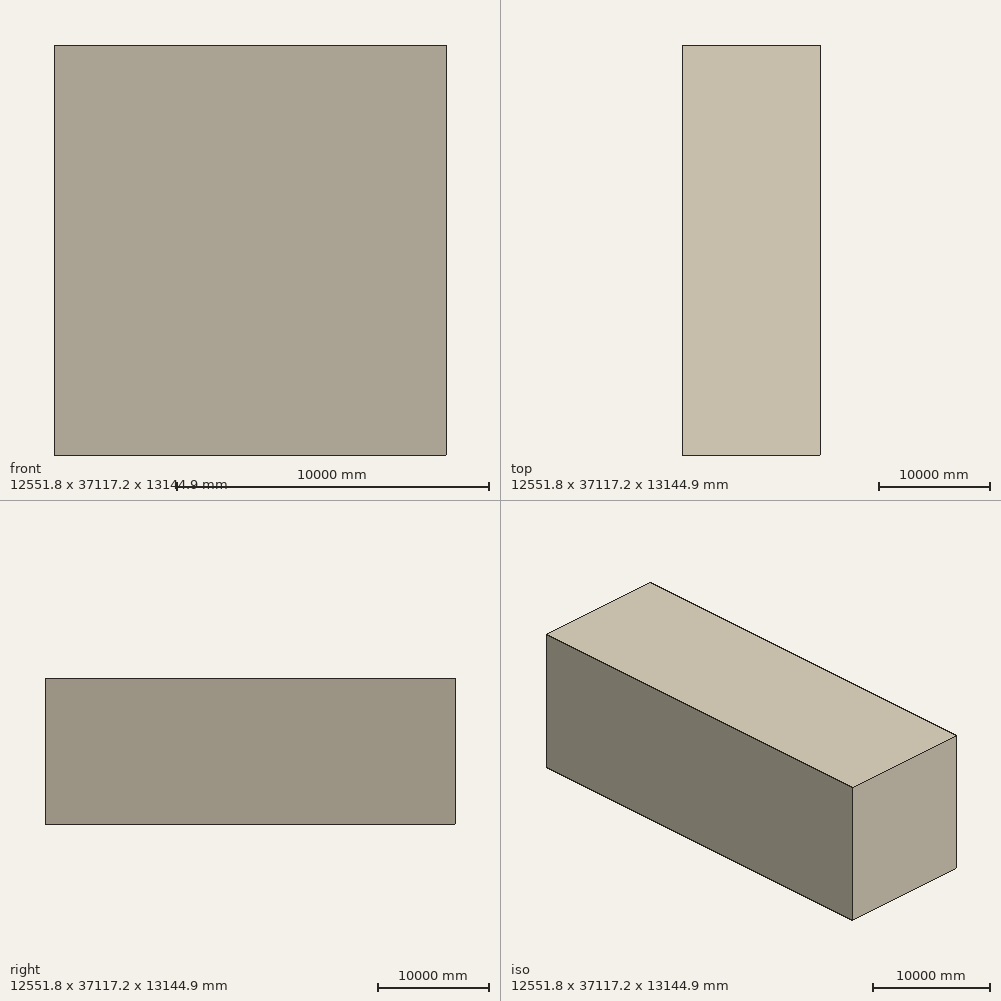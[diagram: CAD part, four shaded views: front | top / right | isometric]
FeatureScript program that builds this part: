
annotation { "Feature Type Name" : "Feature", "Feature Type Description" : "" }
export const myFeature = defineFeature(function(context is Context, id is Id, definition is map)
    precondition{}
    {
        {
            var Q0;
            Q0=qCreatedBy(makeId("Top.planeOp"),FACE);
            var sketch = newSketch(context, id + "F0", { "sketchPlane" : qUnion([Q0])});
            skLineSegment(sketch, "E0.bottom", {"start": v(6275.88, 18558.6) * mm, "end": v(-6275.88, 18558.6) * mm});
            skLineSegment(sketch, "E0.top", {"start": v(6275.88, -18558.6) * mm, "end": v(-6275.88, -18558.6) * mm});
            skLineSegment(sketch, "E0.left", {"start": v(6275.88, -18558.6) * mm, "end": v(6275.88, 18558.6) * mm});
            skLineSegment(sketch, "E0.right", {"start": v(-6275.88, -18558.6) * mm, "end": v(-6275.88, 18558.6) * mm});
            skPoint(sketch, "E0.middle", {"position": v(0, 0) * mm});
            skSolve(sketch);
        }
        {
            var Q0;
            Q0=makeQuery(id+"F0.imprint","IMPRINT",FACE,{"disambiguationData":[TD([[makeQuery(id+"F0.imprint","IMPRINT",EDGE,{"derivedFrom":sQuery(id+"F0.wireOp",EDGE,"E0.bottom")}),1.0]])]});
            extrude(context, id + "F1", {"entities" : qUnion([Q0]), "depth" : 13144.93 * mm});
        }
    });
